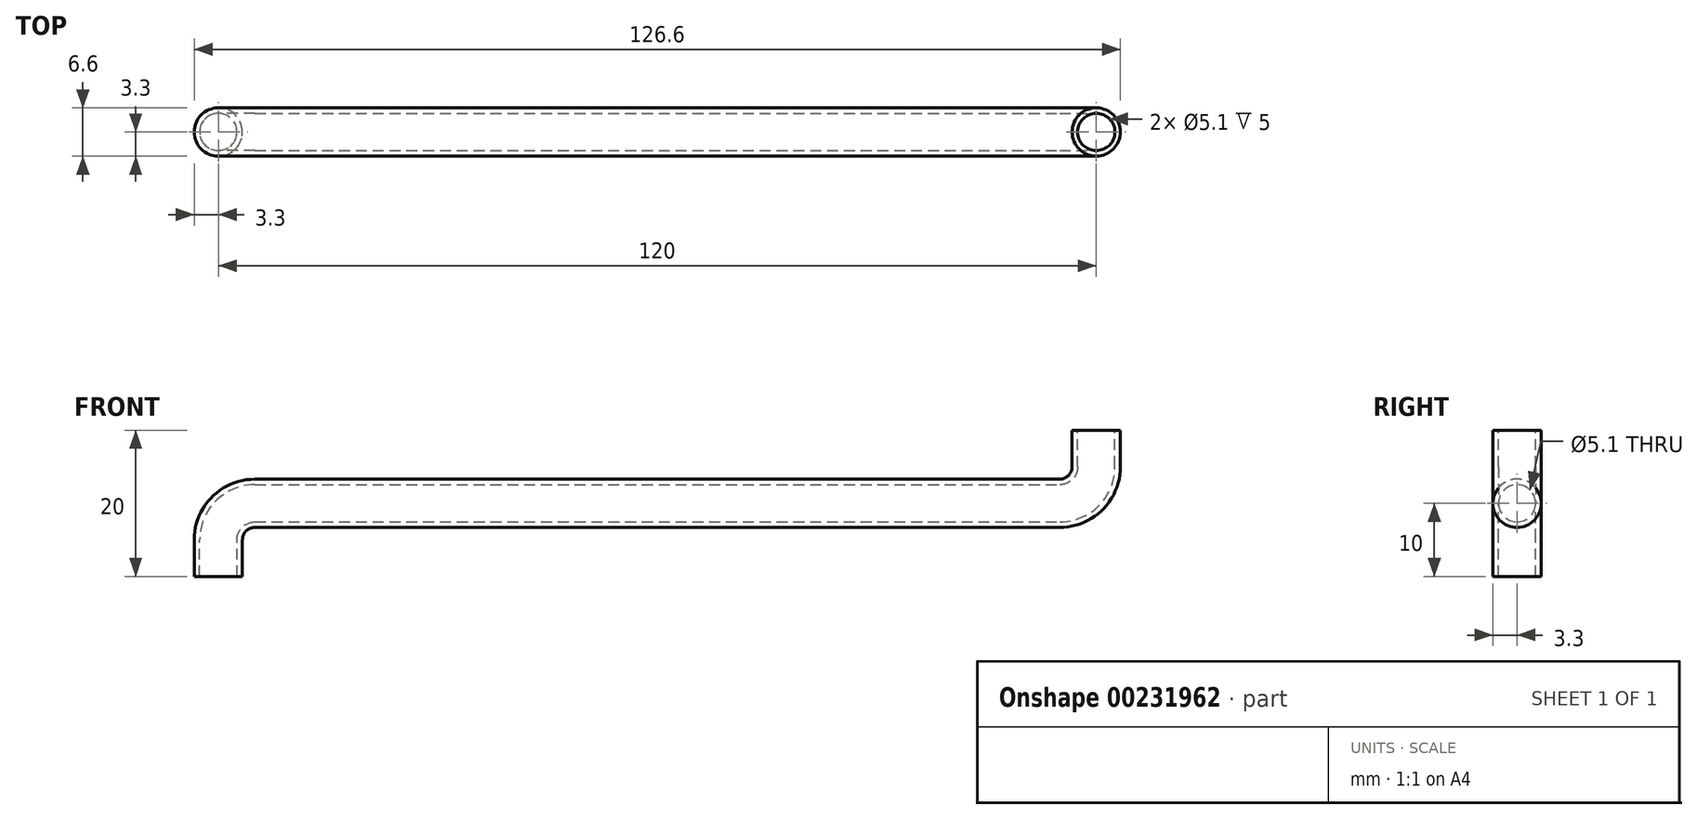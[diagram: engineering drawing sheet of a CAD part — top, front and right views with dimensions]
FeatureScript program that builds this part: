
annotation { "Feature Type Name" : "Feature", "Feature Type Description" : "" }
export const myFeature = defineFeature(function(context is Context, id is Id, definition is map)
    precondition{}
    {
        {
            var Q0;
            Q0=qCreatedBy(makeId("Front.planeOp"),FACE);
            var sketch = newSketch(context, id + "F0", { "sketchPlane" : qUnion([Q0])});
            skLineSegment(sketch, "E0", {"start": v(0, 0) * mm, "end": v(0, 5) * mm});
            skLineSegment(sketch, "E1", {"start": v(5, 10) * mm, "end": v(115, 10) * mm});
            skLineSegment(sketch, "E2", {"start": v(120, 15) * mm, "end": v(120, 20) * mm});
            skPoint(sketch, "E3.visualSharp", {"position": v(0, 10) * mm});
            skArc(sketch, "E3.filletArc", {"start": v(5, 10) * mm, "mid": v(1.46, 8.54) * mm, "end": v(0, 5) * mm});
            skPoint(sketch, "E4.visualSharp", {"position": v(120, 10) * mm});
            skArc(sketch, "E4.filletArc", {"start": v(115, 10) * mm, "mid": v(118.54, 11.46) * mm, "end": v(120, 15) * mm});
            skSolve(sketch);
        }
        {
            var Q0;
            Q0=qCreatedBy(makeId("Top.planeOp"),FACE);
            var sketch = newSketch(context, id + "F1", { "sketchPlane" : qUnion([Q0])});
            skCircle(sketch, "E5", {"center": v(0, 0) * mm, "radius": 2.55 * mm});
            skCircle(sketch, "E6", {"center": v(0, 0) * mm, "radius": 3.3 * mm});
            skSolve(sketch);
        }
        {
            var Q0;
            Q0=makeQuery(id+"F1.imprint","IMPRINT",FACE,{"disambiguationData":[TD([[makeQuery(id+"F1.imprint","IMPRINT",EDGE,{"derivedFrom":sQuery(id+"F1.wireOp",EDGE,"E5")}),-1.0]])]});
            var Q1;
            Q1 = qConstructionFilter(qBodyType(qCreatedBy(id + "F0" ,EDGE), BodyType.WIRE), ConstructionObject.NO);
            sweep(context, id + "F2", {"profiles" : qUnion([Q0]), "path" : qUnion([Q1])});
        }
    });
